# Revit family: ASSA_ABLOY_RD200
name_source: partatom
category: Doors
units: mm (PartAtom-declared; Revit-internal decimal feet)

## family parameters
Always vertical = Yes
Cut with Voids When Loaded = No
Host = Wall
Room Calculation Point = No
Shared = No

## types (1)
- Orion RD200
    AccessoryOptions = Contact manufacturer
    Analytic Construction = <None>
    AntiFingerTrapRequirement = No
    BreakoutFacility = No
    Burglar resistance = EN 1627 class RC2/RC3
    CanopyHeightOptions = 200 - 1200 mm
    Capacity = ?
    Colour = Customer specific
    Cost = 0 $
    Default Elevation = 0 mm  [stored 0 ft]
    Define Thermal Properties by = Schematic Type
    Description = Automatic revolving door system
    DiameterOptions = 1800 - 4000 mm
    DoorIncluded = Yes
    DoorSeal = Yes
    DoorWingOptions = Centerless
    DoorsetFasteners = Screws
    DoorsetOperation = Automatic
    DoorsetOptions = Nigh Closing doors outer/inner
    DrumWallOptions = Glass, Sandwich panel
    ElectronicLock = Yes
    FireExit = No
    FrameFinishOptions = Powder coated, Anodized, Clad in stainless steel, etc.
    FrameProfile = Aluminium
    FrameSeal = Yes
    GlassLayers = 0
    GlassThickness1 = 8.76 mm
    GlassThickness2 = 14.28 mm
    GlassType = Depends on application
    HandicapAccessible = Yes
    HasDrive = Yes
    IsExternal = Yes
    LeafColourOptions = All RAL, customer specific
    Manufacturer = ASSA ABLOY/Record
    ManufacturerURL = http://www.assaabloyentrance.com
    Material = Aluminum
    Model = RD200-4-5 / RD200-3-5
    ModelReference = Depends on the configuration
    NominalHeight = 0 mm  [stored 0 ft]
    NominalLength = 0 mm  [stored 0 ft]
    NominalWidth = 0 mm  [stored 0 ft]
    OperatingTemperature = -20C (-4F) to +50C (113F)
    PassageWidthOptions = ?
    Power Consumption = Revolving Doors complete (100-240V, 50/60 Hz)
    ReferenceStandard = EN16361:2016, EN16005, IEC/EN 60335-1, IEC/EN 60335-2-103, EN13849-1, EN 61000-6-2 EN  61000-6-3, EN 1627:2011 Class RC2, RC3,
    ReplacementCost = Depends on the configuration and door type
    SafetyDevices = Fully compliant with EN16005 and EN ISO 13849-1
    SelfClosing = Yes
    ServiceLifeDuration = ?
    Shape = Cylinder shaped
    ThresholdRequired = No
    URL = https://www.assaabloyentrance.com
    Uniclass2 = ?
    WarrantyDescription = Depends on country
    Weight = Depends on configuration and size

note: [stored X ft] marks values corroborated as IEEE doubles in the binary element streams (Revit-internal decimal feet)

## geometry (parser evidence)
native form markers: Blend x20, Sweep x38
no freeform markers — native parametric forms only
